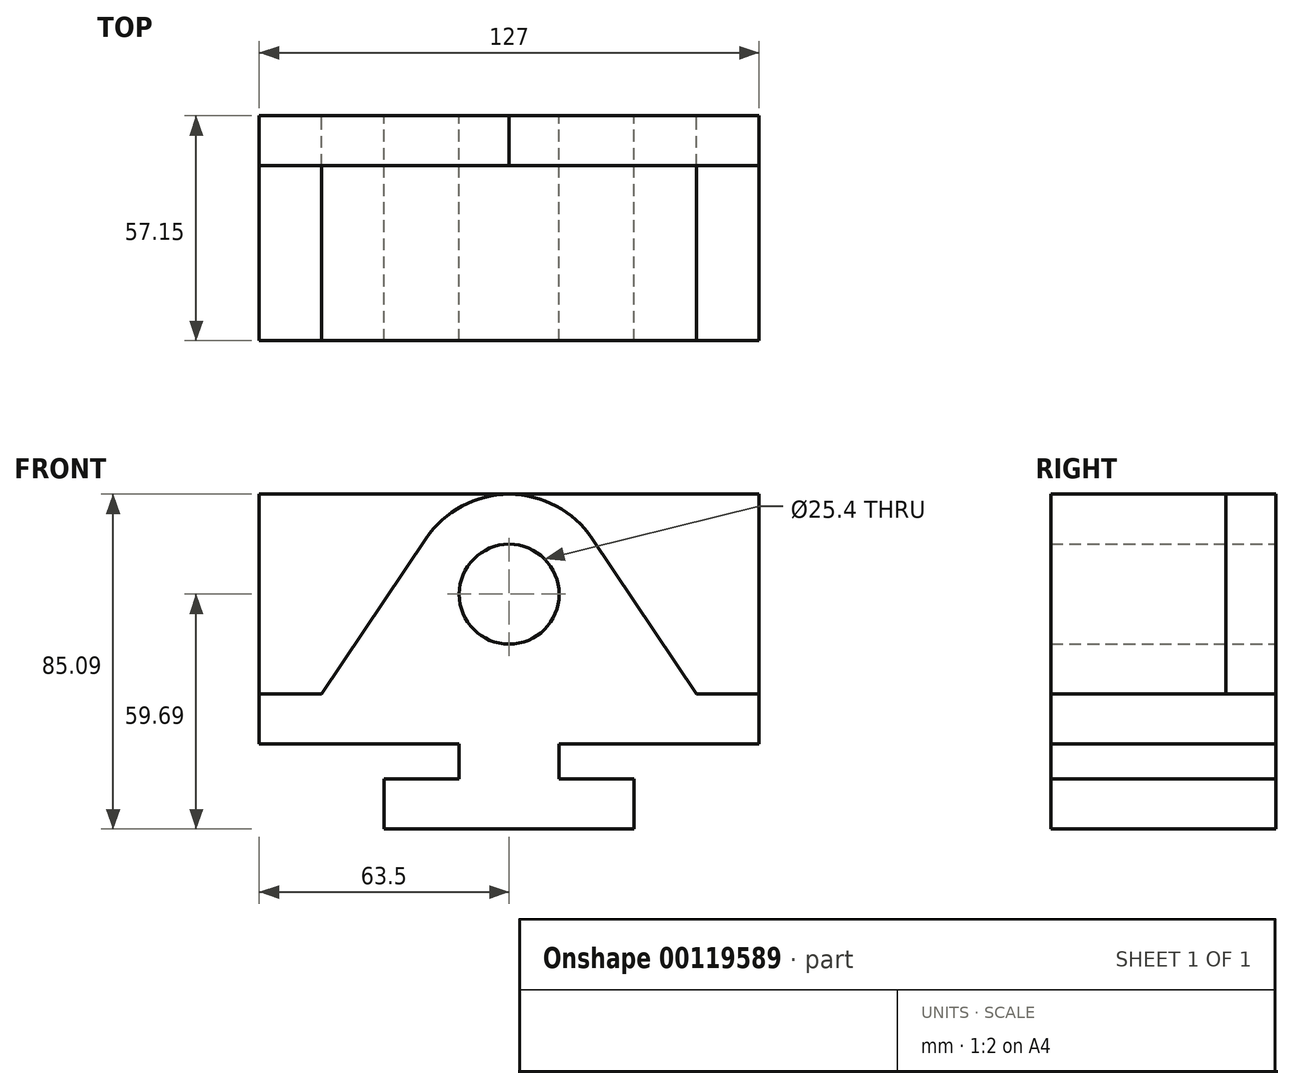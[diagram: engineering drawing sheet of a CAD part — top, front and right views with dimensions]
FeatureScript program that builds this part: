
annotation { "Feature Type Name" : "Feature", "Feature Type Description" : "" }
export const myFeature = defineFeature(function(context is Context, id is Id, definition is map)
    precondition{}
    {
        {
            var Q0;
            Q0=qCreatedBy(makeId("Front.planeOp"),FACE);
            var sketch = newSketch(context, id + "F0", { "sketchPlane" : qUnion([Q0])});
            skLineSegment(sketch, "E0", {"start": v(0, 0) * mm, "end": v(0, 12.7) * mm});
            skLineSegment(sketch, "E1", {"start": v(0, 12.7) * mm, "end": v(19.05, 12.7) * mm});
            skLineSegment(sketch, "E2", {"start": v(19.05, 12.7) * mm, "end": v(19.05, 21.59) * mm});
            skLineSegment(sketch, "E3", {"start": v(19.05, 21.59) * mm, "end": v(-31.75, 21.59) * mm});
            skLineSegment(sketch, "E4", {"start": v(-31.75, 21.6) * mm, "end": v(-31.75, 85.1) * mm});
            skLineSegment(sketch, "E5", {"start": v(-31.75, 85.1) * mm, "end": v(95.25, 85.1) * mm});
            skLineSegment(sketch, "E6", {"start": v(95.25, 85.1) * mm, "end": v(95.25, 21.6) * mm});
            skLineSegment(sketch, "E7", {"start": v(95.25, 21.6) * mm, "end": v(44.45, 21.6) * mm});
            skLineSegment(sketch, "E8", {"start": v(44.45, 21.59) * mm, "end": v(44.45, 12.7) * mm});
            skLineSegment(sketch, "E9", {"start": v(44.45, 12.7) * mm, "end": v(63.5, 12.7) * mm});
            skLineSegment(sketch, "E10", {"start": v(63.5, 12.7) * mm, "end": v(63.5, 0) * mm});
            skLineSegment(sketch, "E11", {"start": v(63.5, 0) * mm, "end": v(0, 0) * mm});
            skLineSegment(sketch, "E12", {"start": v(31.75, 0) * mm, "end": v(31.75, 85.1) * mm, "construction": true});
            skLineSegment(sketch, "E13", {"start": v(-31.75, 34.3) * mm, "end": v(-15.88, 34.3) * mm});
            skLineSegment(sketch, "E14", {"start": v(-15.88, 34.3) * mm, "end": v(10.66, 73.84) * mm});
            skLineSegment(sketch, "E15", {"start": v(95.25, 34.3) * mm, "end": v(79.38, 34.3) * mm});
            skLineSegment(sketch, "E16", {"start": v(79.38, 34.3) * mm, "end": v(52.84, 73.84) * mm});
            skArc(sketch, "E17", {"start": v(52.84, 73.84) * mm, "mid": v(31.75, 85.1) * mm, "end": v(10.66, 73.84) * mm});
            skCircle(sketch, "E18", {"center": v(31.75, 59.7) * mm, "radius": 12.7 * mm});
            skSolve(sketch);
        }
        {
            var Q0;
            {var subQ4=sQuery(id+"F0.wireOp",EDGE,"E13");Q0=makeQuery(id+"F0.imprint","IMPRINT",FACE,{"disambiguationData":[TD([[makeQuery(id+"F0.imprint","IMPRINT",EDGE,{"derivedFrom":subQ4}),1.0]])]});}
            var Q1;
            {var subQ6=sQuery(id+"F0.wireOp",EDGE,"E15");Q1=makeQuery(id+"F0.imprint","IMPRINT",FACE,{"disambiguationData":[TD([[makeQuery(id+"F0.imprint","IMPRINT",EDGE,{"derivedFrom":subQ6}),-1.0]])]});}
            extrude(context, id + "F1", {"entities" : qUnion([Q0, Q1]), "depth" : 12.7 * mm});
        }
        {
            var Q0;
            Q0=makeQuery(id+"F0.imprint","IMPRINT",FACE,{"disambiguationData":[TD([[makeQuery(id+"F0.imprint","IMPRINT",EDGE,{"derivedFrom":sQuery(id+"F0.wireOp",EDGE,"E0")}),-1.0]])]});
            extrude(context, id + "F2", {"entities" : qUnion([Q0]), "depth" : 57.15 * mm});
        }
    });
